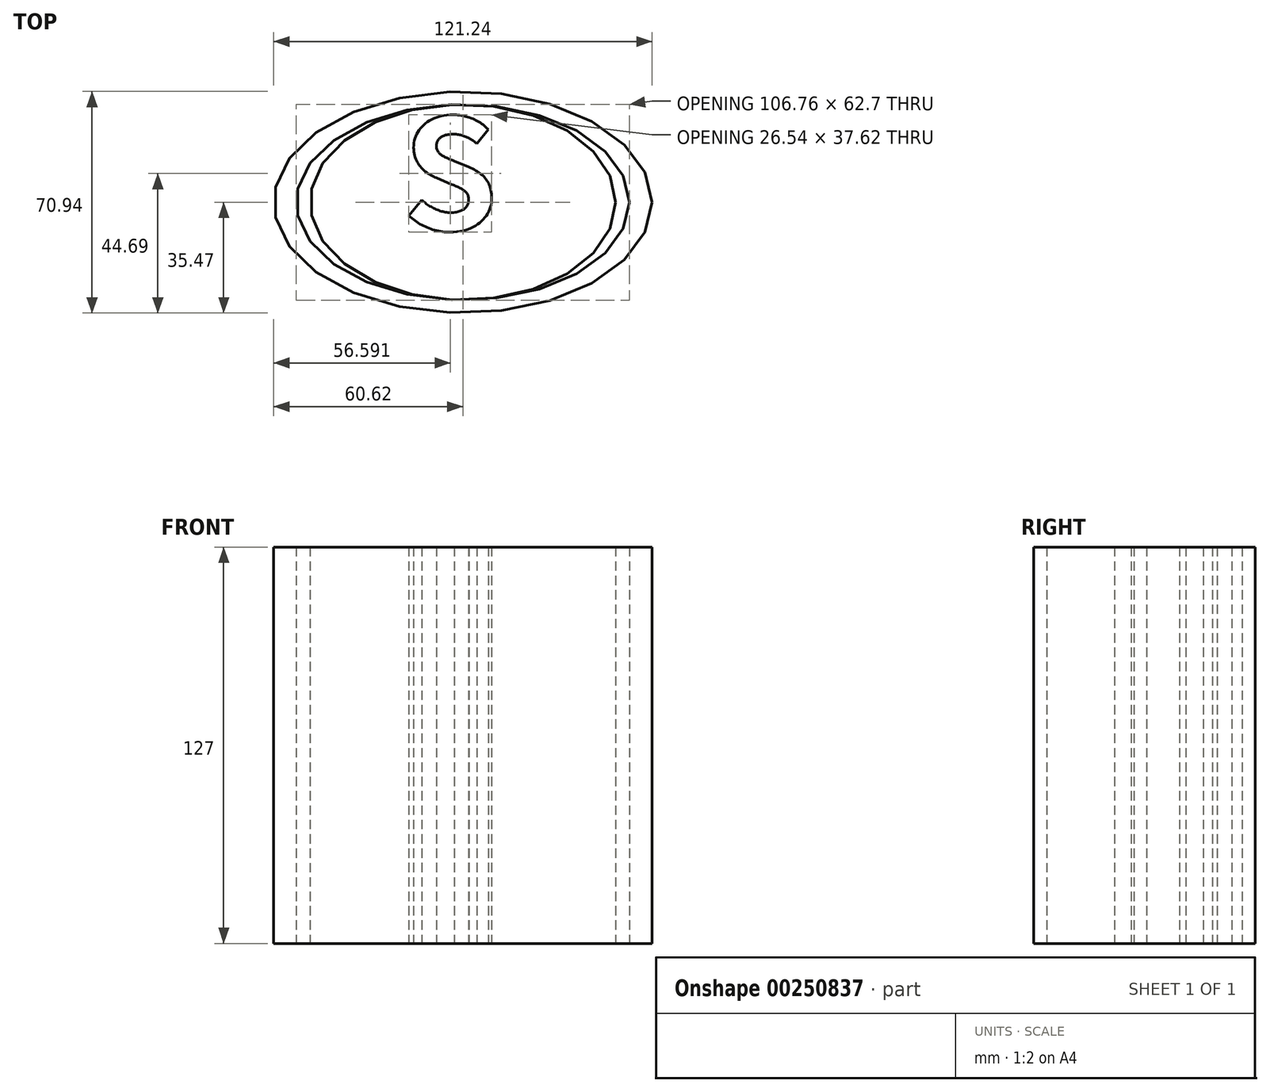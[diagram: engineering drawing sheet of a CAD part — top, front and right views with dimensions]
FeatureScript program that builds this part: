
annotation { "Feature Type Name" : "Feature", "Feature Type Description" : "" }
export const myFeature = defineFeature(function(context is Context, id is Id, definition is map)
    precondition{}
    {
        {
            var Q0;
            Q0=qCreatedBy(makeId("Top.planeOp"),FACE);
            var sketch = newSketch(context, id + "F0", { "sketchPlane" : qUnion([Q0])});
            skEllipse(sketch, "E0", {"center": v(0, 0) * mm, "majorRadius": 60.62 * mm, "minorRadius": 35.47 * mm, "majorAxis": v(1, 0)});
            skEllipse(sketch, "E1", {"center": v(0, 0) * mm, "majorRadius": 53.38 * mm, "minorRadius": 31.35 * mm, "majorAxis": v(1, 0)});
            skEllipse(sketch, "E2", {"center": v(0, 0) * mm, "majorRadius": 48.93 * mm, "minorRadius": 31.33 * mm, "majorAxis": v(1, 0)});
            skText(sketch, "E3", { "text": "S", "fontName": "NotoSansCJKjp-Bold.otf"});
            const initialGuessF0  = {"E3": [-0.01936, -0.0089, 1, 0, 0.03526]};
            skSetInitialGuess(sketch, initialGuessF0);
            skSolve(sketch);
        }
        {
            var Q0;
            Q0 = qSketchRegion(id + "F0", true);
            var Q1;
            Q1=makeQuery(id+"F0.imprint","IMPRINT",FACE,{"disambiguationData":[TD([[makeQuery(id+"F0.imprint","IMPRINT",EDGE,{"derivedFrom":sQuery(id+"F0.wireOp",EDGE,"E2")}),1.0]])]});
            extrude(context, id + "F1", {"entities" : qUnion([Q0, Q1]), "depth" : 127 * mm});
        }
    });
